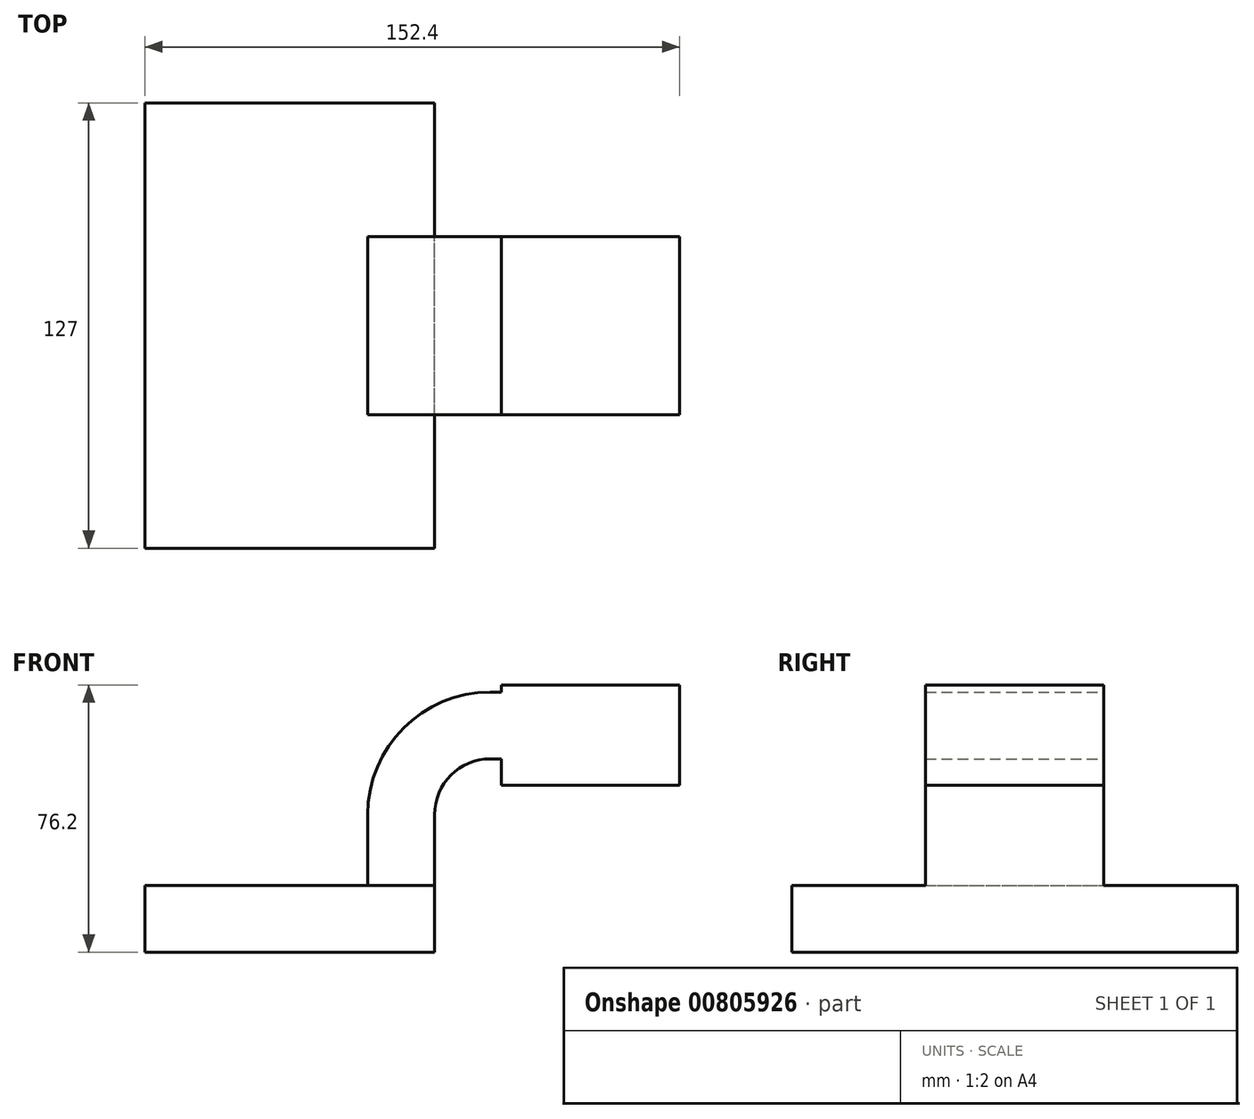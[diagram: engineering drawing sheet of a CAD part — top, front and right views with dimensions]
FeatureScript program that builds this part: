
annotation { "Feature Type Name" : "Feature", "Feature Type Description" : "" }
export const myFeature = defineFeature(function(context is Context, id is Id, definition is map)
    precondition{}
    {
        {
            var Q0;
            Q0=qCreatedBy(makeId("Front.planeOp"),FACE);
            var sketch = newSketch(context, id + "F0", { "sketchPlane" : qUnion([Q0])});
            skLineSegment(sketch, "E0.bottom", {"start": v(41.28, -9.52) * mm, "end": v(-41.28, -9.53) * mm});
            skLineSegment(sketch, "E0.top", {"start": v(41.28, 9.53) * mm, "end": v(-41.28, 9.53) * mm});
            skLineSegment(sketch, "E0.left", {"start": v(41.28, -9.52) * mm, "end": v(41.28, 9.53) * mm});
            skLineSegment(sketch, "E0.right", {"start": v(-41.28, -9.53) * mm, "end": v(-41.28, 9.53) * mm});
            skPoint(sketch, "E0.middle", {"position": v(0, 0) * mm});
            skLineSegment(sketch, "E1.bottom", {"start": v(111.12, 38.1) * mm, "end": v(60.32, 38.1) * mm});
            skLineSegment(sketch, "E1.top", {"start": v(111.12, 66.68) * mm, "end": v(60.32, 66.68) * mm});
            skLineSegment(sketch, "E1.left", {"start": v(111.12, 38.1) * mm, "end": v(111.12, 66.68) * mm});
            skLineSegment(sketch, "E1.right", {"start": v(60.32, 38.1) * mm, "end": v(60.32, 66.68) * mm});
            skPoint(sketch, "E1.middle", {"position": v(85.72, 52.39) * mm});
            skLineSegment(sketch, "E2", {"start": v(41.28, 9.53) * mm, "end": v(41.28, 29.7) * mm});
            skArc(sketch, "E3", {"start": v(41.27, 29.7) * mm, "mid": v(45.92, 40.92) * mm, "end": v(57.15, 45.57) * mm});
            skLineSegment(sketch, "E4", {"start": v(57.15, 45.57) * mm, "end": v(85.72, 45.57) * mm});
            skPoint(sketch, "E4.endSnap0", {"position": v(85.72, 38.1) * mm});
            skLineSegment(sketch, "E5.0", {"start": v(57.15, 64.62) * mm, "end": v(85.72, 64.62) * mm});
            skArc(sketch, "E5.1", {"start": v(22.23, 29.7) * mm, "mid": v(32.45, 54.4) * mm, "end": v(57.15, 64.62) * mm});
            skLineSegment(sketch, "E5.2", {"start": v(22.22, 9.53) * mm, "end": v(22.22, 29.7) * mm});
            skLineSegment(sketch, "E6", {"start": v(85.72, 38.1) * mm, "end": v(85.72, 66.68) * mm});
            skFitSpline(sketch, "E7", {"points": [v(-41.28, 9.52) * mm, v(57.15, 64.62) * mm], "startDerivative": vector(95.46, 115.47) * mm, "endDerivative": vector(122.31, -5.22) * mm});
            skSolve(sketch);
        }
        {
            var Q0;
            Q0=makeQuery(id+"F0.imprint","IMPRINT",FACE,{"disambiguationData":[TD([[makeQuery(id+"F0.imprint","IMPRINT",EDGE,{"derivedFrom":sQuery(id+"F0.wireOp",EDGE,"E0.bottom")}),-1.0]])]});
            extrude(context, id + "F1", {"entities" : qUnion([Q0]), "endBound" : BoundingType.SYMMETRIC, "depth" : 127 * mm, "offsetDistance" : 25.4 * mm});
        }
        {
            var Q0;
            {var subQ1=sQuery(id+"F0.wireOp",EDGE,"E2");Q0=makeQuery(id+"F0.imprint","IMPRINT",FACE,{"disambiguationData":[TD([[makeQuery(id+"F0.imprint","IMPRINT",EDGE,{"derivedFrom":subQ1}),1.0]])]});}
            var Q1;
            {var subQ4=sQuery(id+"F0.wireOp",EDGE,"E1.left");Q1=makeQuery(id+"F0.imprint","IMPRINT",FACE,{"disambiguationData":[TD([[makeQuery(id+"F0.imprint","IMPRINT",EDGE,{"derivedFrom":subQ4}),1.0]])]});}
            var Q2;
            {var subQ0=sQuery(id+"F0.wireOp",EDGE,"E4");var subQ1=sQuery(id+"F0.wireOp",EDGE,"E1.right");var subQ2=makeQuery(id+"F0.imprint","INTERSECT",VERTEX,{"derivedFrom":[subQ1,subQ0]});Q2=makeQuery(id+"F0.imprint","IMPRINT",FACE,{"disambiguationData":[TD([[makeQuery(id+"F0.imprint","IMPRINT",EDGE,{"disambiguationData":[TD([[subQ2,-1.0]])],"derivedFrom":subQ1}),-1.0]])]});}
            var Q3;
            {var subQ0=sQuery(id+"F0.wireOp",EDGE,"E1.right");var subQ1=sQuery(id+"F0.wireOp",EDGE,"E1.bottom");var subQ2=makeQuery(id+"F0.imprint","INTERSECT",VERTEX,{"derivedFrom":[subQ1,subQ0]});Q3=makeQuery(id+"F0.imprint","IMPRINT",FACE,{"disambiguationData":[TD([[makeQuery(id+"F0.imprint","IMPRINT",EDGE,{"disambiguationData":[TD([[subQ2,1.0]])],"derivedFrom":subQ1}),-1.0]])]});}
            var Q4;
            {var subQ0=sQuery(id+"F0.wireOp",EDGE,"E1.right");var subQ1=sQuery(id+"F0.wireOp",EDGE,"E1.top");var subQ2=makeQuery(id+"F0.imprint","INTERSECT",VERTEX,{"derivedFrom":[subQ1,subQ0]});Q4=makeQuery(id+"F0.imprint","IMPRINT",FACE,{"disambiguationData":[TD([[makeQuery(id+"F0.imprint","IMPRINT",EDGE,{"disambiguationData":[TD([[subQ2,1.0]])],"derivedFrom":subQ1}),1.0]])]});}
            extrude(context, id + "F2", {"entities" : qUnion([Q0, Q1, Q2, Q3, Q4]), "operationType" : NewBodyOperationType.ADD, "endBound" : BoundingType.SYMMETRIC, "depth" : 50.8 * mm, "offsetDistance" : 25.4 * mm});
        }
        {
            var Q0;
            Q0=makeQuery(id+"F0.imprint","IMPRINT",FACE,{"disambiguationData":[TD([[makeQuery(id+"F0.imprint","IMPRINT",EDGE,{"derivedFrom":sQuery(id+"F0.wireOp",EDGE,"E5.1")}),1.0]])]});
            extrude(context, id + "F3", {"entities" : qUnion([Q0]), "operationType" : NewBodyOperationType.ADD, "endBound" : BoundingType.SYMMETRIC, "depth" : 15.88 * mm, "offsetDistance" : 25.4 * mm});
        }
    });
